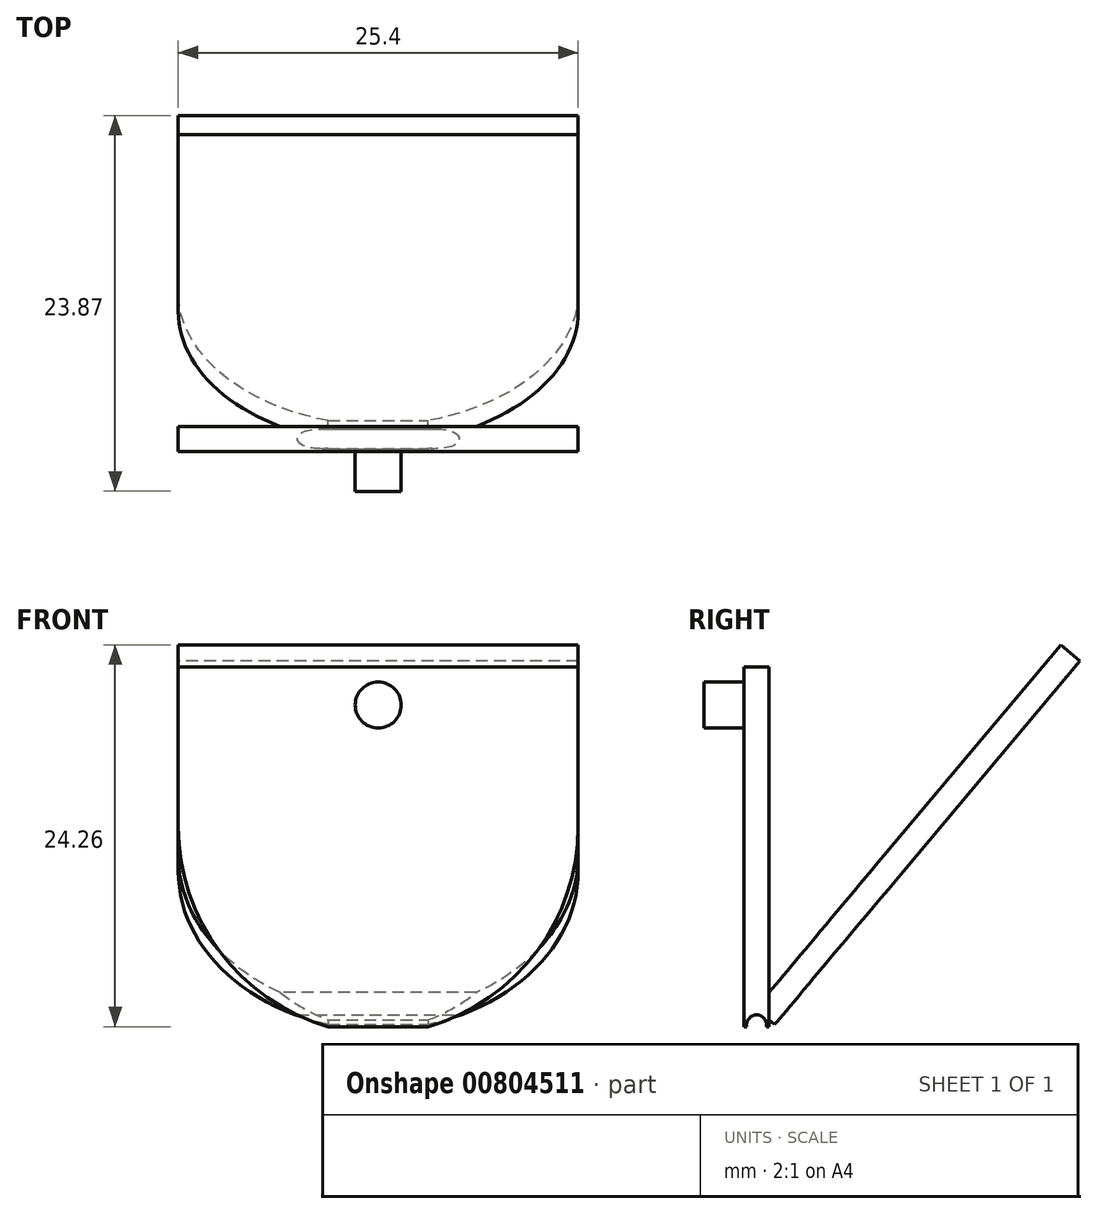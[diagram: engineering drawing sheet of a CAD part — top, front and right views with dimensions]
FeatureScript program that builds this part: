
annotation { "Feature Type Name" : "Feature", "Feature Type Description" : "" }
export const myFeature = defineFeature(function(context is Context, id is Id, definition is map)
    precondition{}
    {
        {
            var Q0;
            Q0=qCreatedBy(makeId("Front.planeOp"),FACE);
            var sketch = newSketch(context, id + "F0", { "sketchPlane" : qUnion([Q0])});
            skLineSegment(sketch, "E0", {"start": v(-12.7, -1.38) * mm, "end": v(-12.7, 8.78) * mm});
            skLineSegment(sketch, "E1", {"start": v(-12.7, 8.78) * mm, "end": v(12.7, 8.78) * mm});
            skLineSegment(sketch, "E2", {"start": v(12.7, 8.78) * mm, "end": v(12.7, -1.38) * mm});
            skLineSegment(sketch, "E3", {"start": v(0, -14.08) * mm, "end": v(31.56, -14.08) * mm, "construction": true});
            skLineSegment(sketch, "E4", {"start": v(0, -14.08) * mm, "end": v(3.18, -14.08) * mm});
            skLineSegment(sketch, "E5", {"start": v(3.18, -14.08) * mm, "end": v(-3.17, -14.08) * mm});
            skArc(sketch, "E6", {"start": v(-12.7, -1.38) * mm, "mid": v(-10.05, -9.32) * mm, "end": v(-3.17, -14.08) * mm});
            skArc(sketch, "E7", {"start": v(3.18, -14.08) * mm, "mid": v(10.05, -9.32) * mm, "end": v(12.7, -1.38) * mm});
            skSolve(sketch);
        }
        {
            var Q0;
            Q0=sQuery(id+"F0.wireOp",EDGE,"E3");
            cPlane(context, id + "F1", {"entities" : qUnion([Q0]), "cplaneType" : CPlaneType.LINE_ANGLE, "offset" : 25.4 * mm, "angle" : 40 * degree, "oppositeDirection" : true, "width" : 152.4 * mm, "height" : 152.4 * mm});
        }
        {
            var Q0;
            Q0=qCreatedBy(id+"F1.planeOp",FACE);
            var sketch = newSketch(context, id + "F2", { "sketchPlane" : qUnion([Q0])});
            skLineSegment(sketch, "E8", {"start": v(-12.7, 2.75) * mm, "end": v(-12.7, 15.45) * mm});
            skLineSegment(sketch, "E9", {"start": v(-12.7, 15.45) * mm, "end": v(12.7, 15.45) * mm});
            skLineSegment(sketch, "E10", {"start": v(12.7, 15.45) * mm, "end": v(12.7, 2.75) * mm});
            skLineSegment(sketch, "E11", {"start": v(0, -9.95) * mm, "end": v(31.56, -9.95) * mm, "construction": true});
            skLineSegment(sketch, "E12", {"start": v(0, -9.95) * mm, "end": v(3.17, -9.95) * mm});
            skLineSegment(sketch, "E13", {"start": v(3.17, -9.95) * mm, "end": v(-3.18, -9.95) * mm});
            skArc(sketch, "E14", {"start": v(-12.7, 2.75) * mm, "mid": v(-10.06, -5.18) * mm, "end": v(-3.18, -9.95) * mm});
            skArc(sketch, "E15", {"start": v(3.17, -9.95) * mm, "mid": v(10.05, -5.18) * mm, "end": v(12.7, 2.75) * mm});
            skLineSegment(sketch, "E16", {"start": v(0, 2.75) * mm, "end": v(0, -9.95) * mm, "construction": true});
            skLineSegment(sketch, "E17", {"start": v(0, -9.95) * mm, "end": v(-3.18, -9.95) * mm, "construction": true});
            skLineSegment(sketch, "E18", {"start": v(-3.18, -9.95) * mm, "end": v(3.17, -9.95) * mm, "construction": true});
            skLineSegment(sketch, "E19", {"start": v(-12.7, 2.75) * mm, "end": v(-12.7, 20.22) * mm});
            skLineSegment(sketch, "E20", {"start": v(-12.7, 20.22) * mm, "end": v(12.7, 20.22) * mm});
            skLineSegment(sketch, "E21", {"start": v(12.7, 20.22) * mm, "end": v(12.7, 2.75) * mm});
            skSolve(sketch);
        }
        {
            var Q0;
            Q0 = qSketchRegion(id + "F2", true);
            extrude(context, id + "F3", {"entities" : qUnion([Q0]), "endBound" : BoundingType.SYMMETRIC, "oppositeDirection" : true, "depth" : 1.59 * mm, "offsetDistance" : 25.4 * mm});
        }
        {
            var Q0;
            Q0=makeQuery(id+"F0.imprint","IMPRINT",FACE,{"disambiguationData":[TD([[makeQuery(id+"F0.imprint","IMPRINT",EDGE,{"derivedFrom":sQuery(id+"F0.wireOp",EDGE,"E0")}),-1.0]])]});
            extrude(context, id + "F4", {"entities" : qUnion([Q0]), "operationType" : NewBodyOperationType.ADD, "endBound" : BoundingType.SYMMETRIC, "oppositeDirection" : true, "depth" : 1.59 * mm, "offsetDistance" : 25.4 * mm});
        }
        {
            var Q0;
            Q0=qCreatedBy(makeId("Right.planeOp"),FACE);
            var sketch = newSketch(context, id + "F5", { "sketchPlane" : qUnion([Q0])});
            skLineSegment(sketch, "E22", {"start": v(0, 0) * mm, "end": v(0, -13.97) * mm, "construction": true});
            skCircle(sketch, "E23", {"center": v(0, -13.97) * mm, "radius": 0.64 * mm, "construction": true});
            skCircle(sketch, "E24", {"center": v(0, -13.97) * mm, "radius": 0.64 * mm});
            skSolve(sketch);
        }
        {
            var Q0;
            Q0=makeQuery(id+"F5.imprint","IMPRINT",FACE,{"disambiguationData":[TD([[makeQuery(id+"F5.imprint","IMPRINT",EDGE,{"derivedFrom":sQuery(id+"F5.wireOp",EDGE,"E24")}),1.0]])]});
            extrude(context, id + "F6", {"entities" : qUnion([Q0]), "operationType" : NewBodyOperationType.REMOVE, "endBound" : BoundingType.SYMMETRIC, "oppositeDirection" : true, "depth" : 50.8 * mm, "offsetDistance" : 25.4 * mm});
        }
        {
            var Q0;
            Q0=makeQuery(id+"F4.opExtrude","CAP_FACE",FACE,{"disambiguationData":[OSD([sQuery(id+"F0.wireOp",EDGE,"E0"),sQuery(id+"F0.wireOp",EDGE,"E1"),sQuery(id+"F0.wireOp",EDGE,"E2"),sQuery(id+"F0.wireOp",EDGE,"E5"),sQuery(id+"F0.wireOp",EDGE,"E6"),sQuery(id+"F0.wireOp",EDGE,"E7")])],"isStart":true});
            var sketch = newSketch(context, id + "F7", { "sketchPlane" : qUnion([Q0])});
            skLineSegment(sketch, "E25", {"start": v(0, 0) * mm, "end": v(0, 6.35) * mm});
            skCircle(sketch, "E26", {"center": v(0, 6.35) * mm, "radius": 1.46 * mm});
            skSolve(sketch);
        }
        {
            var Q0;
            Q0=makeQuery(id+"F7.imprint","IMPRINT",FACE,{"disambiguationData":[TD([[makeQuery(id+"F7.imprint","IMPRINT",EDGE,{"derivedFrom":sQuery(id+"F7.wireOp",EDGE,"E26")}),1.0]])]});
            extrude(context, id + "F8", {"entities" : qUnion([Q0]), "operationType" : NewBodyOperationType.ADD, "depth" : 2.54 * mm, "offsetDistance" : 25.4 * mm});
        }
    });
